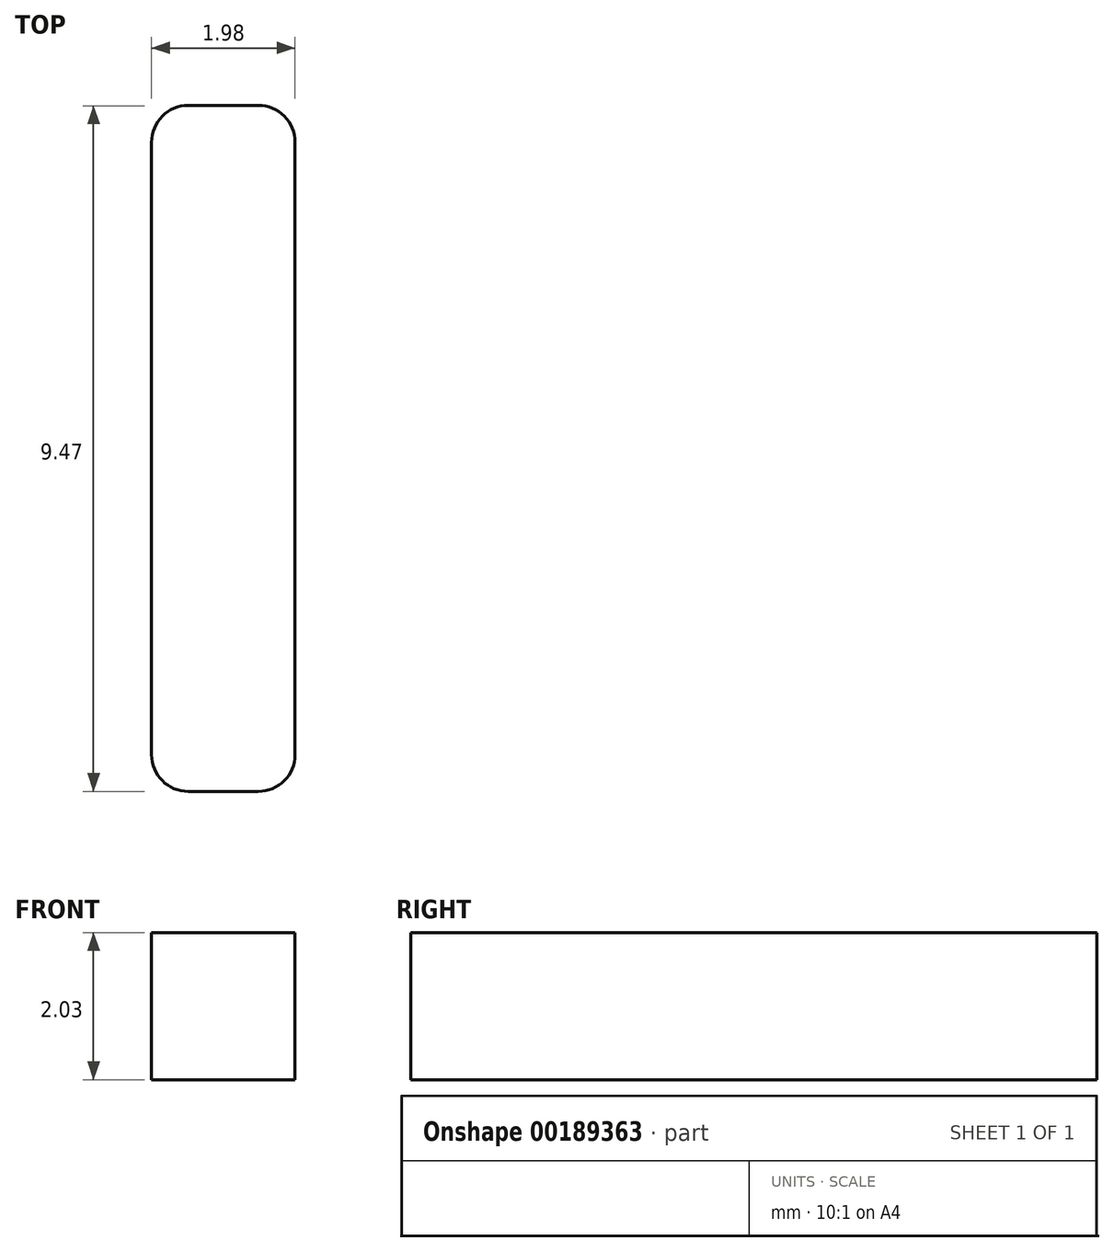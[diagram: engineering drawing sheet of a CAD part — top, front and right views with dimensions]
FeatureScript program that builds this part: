
annotation { "Feature Type Name" : "Feature", "Feature Type Description" : "" }
export const myFeature = defineFeature(function(context is Context, id is Id, definition is map)
    precondition{}
    {
        {
            var Q0;
            Q0=qCreatedBy(makeId("Top.planeOp"),FACE);
            var sketch = newSketch(context, id + "F0", { "sketchPlane" : qUnion([Q0])});
            skLineSegment(sketch, "E0.bottom", {"start": v(0.48, 0) * mm, "end": v(-0.48, 0) * mm});
            skLineSegment(sketch, "E0.top", {"start": v(0.48, 9.47) * mm, "end": v(-0.48, 9.47) * mm});
            skLineSegment(sketch, "E0.left", {"start": v(1, 0.5) * mm, "end": v(1, 8.97) * mm});
            skLineSegment(sketch, "E0.right", {"start": v(-1, 0.5) * mm, "end": v(-1, 8.97) * mm});
            skPoint(sketch, "E1", {"position": v(0, 0) * mm});
            skLineSegment(sketch, "E2", {"start": v(0, -1.94) * mm, "end": v(0, 14.4) * mm, "construction": true});
            skPoint(sketch, "E3.visualSharp", {"position": v(1, 0) * mm});
            skArc(sketch, "E3.filletArc", {"start": v(0.48, 0) * mm, "mid": v(0.84, 0.15) * mm, "end": v(1, 0.5) * mm});
            skPoint(sketch, "E4.visualSharp", {"position": v(-1, 0) * mm});
            skArc(sketch, "E4.filletArc", {"start": v(-1, 0.5) * mm, "mid": v(-0.84, 0.15) * mm, "end": v(-0.48, 0) * mm});
            skPoint(sketch, "E5.visualSharp", {"position": v(-1, 9.47) * mm});
            skArc(sketch, "E5.filletArc", {"start": v(-0.48, 9.47) * mm, "mid": v(-0.84, 9.33) * mm, "end": v(-1, 8.97) * mm});
            skPoint(sketch, "E6.visualSharp", {"position": v(1, 9.47) * mm});
            skArc(sketch, "E6.filletArc", {"start": v(1, 8.97) * mm, "mid": v(0.84, 9.33) * mm, "end": v(0.48, 9.47) * mm});
            skSolve(sketch);
        }
        {
            var Q0;
            Q0 = qSketchRegion(id + "F0", true);
            extrude(context, id + "F1", {"entities" : qUnion([Q0]), "depth" : 2.03 * mm});
        }
    });
